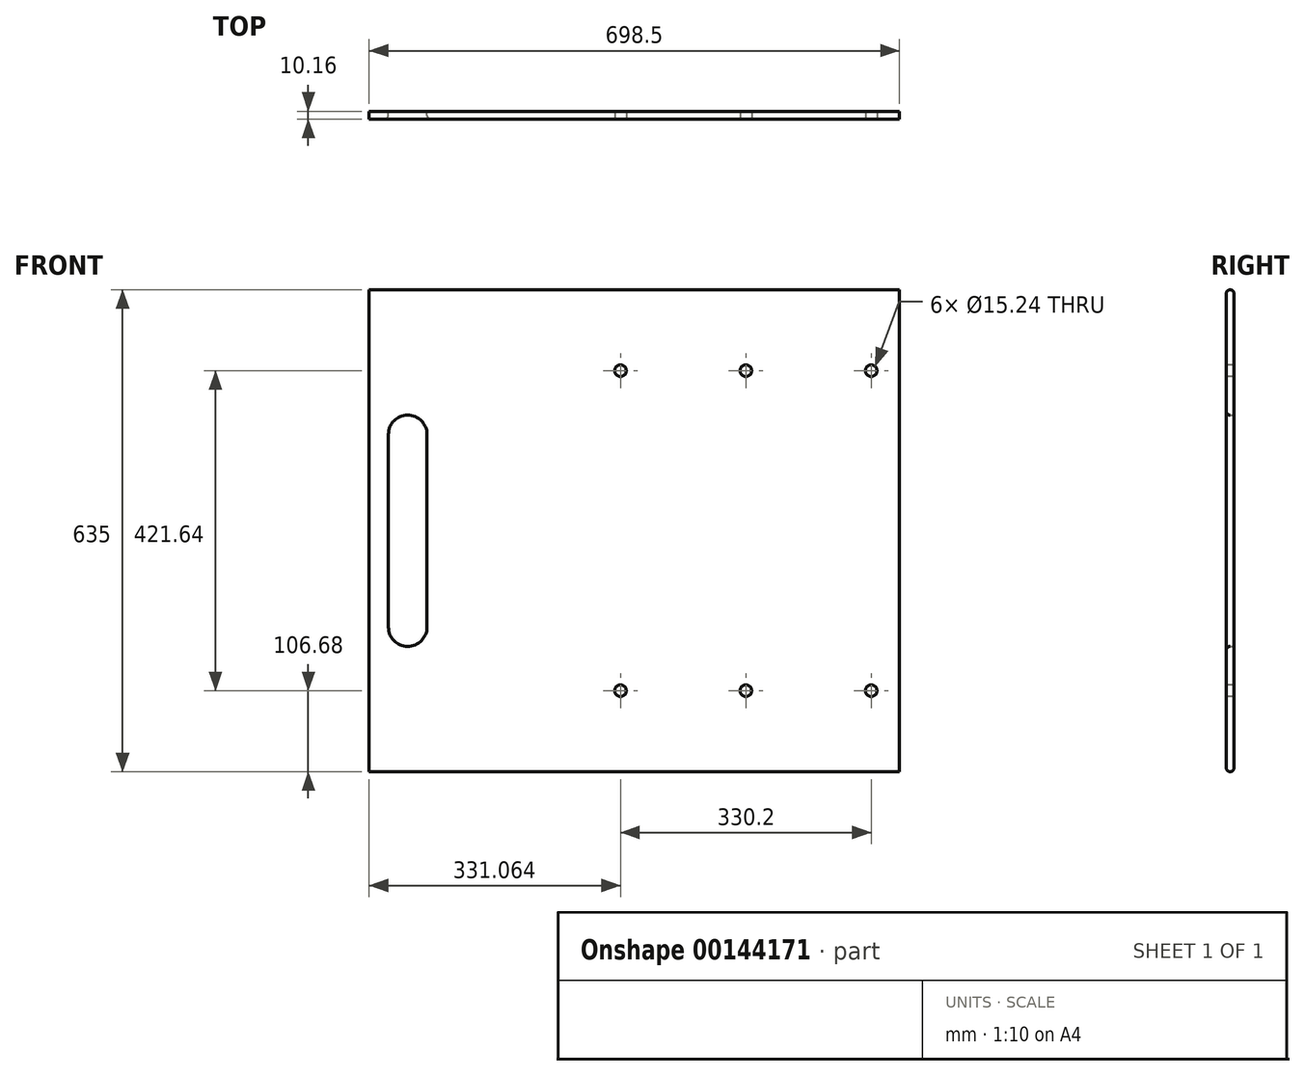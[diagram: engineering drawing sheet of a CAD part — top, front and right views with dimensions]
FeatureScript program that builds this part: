
annotation { "Feature Type Name" : "Feature", "Feature Type Description" : "" }
export const myFeature = defineFeature(function(context is Context, id is Id, definition is map)
    precondition{}
    {
        {
            var Q0;
            Q0=qCreatedBy(makeId("Front.planeOp"),FACE);
            var sketch = newSketch(context, id + "F0", { "sketchPlane" : qUnion([Q0])});
            skLineSegment(sketch, "E0.bottom", {"start": v(0, 0) * mm, "end": v(698.5, 0) * mm});
            skLineSegment(sketch, "E0.top", {"start": v(0, 635) * mm, "end": v(698.5, 635) * mm});
            skLineSegment(sketch, "E0.left", {"start": v(0, 0) * mm, "end": v(0, 635) * mm});
            skLineSegment(sketch, "E0.right", {"start": v(698.5, 0) * mm, "end": v(698.5, 635) * mm});
            skSolve(sketch);
        }
        {
            var Q0;
            Q0=makeQuery(id+"F0.imprint","IMPRINT",FACE,{"disambiguationData":[TD([[makeQuery(id+"F0.imprint","IMPRINT",EDGE,{"derivedFrom":sQuery(id+"F0.wireOp",EDGE,"E0.bottom")}),1.0]])]});
            extrude(context, id + "F1", {"entities" : qUnion([Q0]), "depth" : 10.16 * mm});
        }
        {
            var Q0;
            Q0=makeQuery(id+"F1.opExtrude","CAP_FACE",FACE,{"disambiguationData":[OSD([sQuery(id+"F0.wireOp",EDGE,"E0.bottom"),sQuery(id+"F0.wireOp",EDGE,"E0.top"),sQuery(id+"F0.wireOp",EDGE,"E0.left"),sQuery(id+"F0.wireOp",EDGE,"E0.right")])],"isStart":false});
            var sketch = newSketch(context, id + "F2", { "sketchPlane" : qUnion([Q0])});
            skLineSegment(sketch, "E1", {"start": v(0, 317.5) * mm, "end": v(50.8, 317.5) * mm, "construction": true});
            skLineSegment(sketch, "E2", {"start": v(50.8, 444.5) * mm, "end": v(50.8, 190.5) * mm, "construction": true});
            skArc(sketch, "E3.0.startCap", {"start": v(25.4, 444.5) * mm, "mid": v(50.8, 469.9) * mm, "end": v(76.2, 444.5) * mm});
            skArc(sketch, "E3.0.endCap", {"start": v(76.2, 190.5) * mm, "mid": v(50.8, 165.1) * mm, "end": v(25.4, 190.5) * mm});
            skLineSegment(sketch, "E3.0.left", {"start": v(76.2, 444.5) * mm, "end": v(76.2, 190.5) * mm});
            skLineSegment(sketch, "E3.0.right", {"start": v(25.4, 444.5) * mm, "end": v(25.4, 190.5) * mm});
            skSolve(sketch);
        }
        {
            var Q0;
            Q0=makeQuery(id+"F1.opExtrude","CAP_FACE",FACE,{"disambiguationData":[OSD([sQuery(id+"F0.wireOp",EDGE,"E0.bottom"),sQuery(id+"F0.wireOp",EDGE,"E0.top"),sQuery(id+"F0.wireOp",EDGE,"E0.left"),sQuery(id+"F0.wireOp",EDGE,"E0.right")])],"isStart":true});
            var sketch = newSketch(context, id + "F3", { "sketchPlane" : qUnion([Q0])});
            skLineSegment(sketch, "E4.0", {"start": v(-25.4, 444.5) * mm, "end": v(-25.4, 190.5) * mm});
            skArc(sketch, "E5.0", {"start": v(-25.4, 444.5) * mm, "mid": v(-50.8, 469.9) * mm, "end": v(-76.2, 444.5) * mm});
            skLineSegment(sketch, "E6.0", {"start": v(-76.2, 444.5) * mm, "end": v(-76.2, 190.5) * mm});
            skArc(sketch, "E7.0", {"start": v(-76.2, 190.5) * mm, "mid": v(-50.8, 165.1) * mm, "end": v(-25.4, 190.5) * mm});
            skSolve(sketch);
        }
        {
            var Q0;
            Q0=makeQuery(id+"F3.imprint","IMPRINT",FACE,{"disambiguationData":[TD([[makeQuery(id+"F3.imprint","IMPRINT",EDGE,{"derivedFrom":sQuery(id+"F3.wireOp",EDGE,"E4.0")}),-1.0]])]});
            extrude(context, id + "F4", {"entities" : qUnion([Q0]), "operationType" : NewBodyOperationType.REMOVE, "endBound" : BoundingType.THROUGH_ALL, "oppositeDirection" : true, "depth" : 25.4 * mm});
        }
        {
            var Q0;
            Q0=makeQuery(id+"F4.boolean.opBoolean","COPY",EDGE,{"derivedFrom":makeQuery(id+"F4.opExtrude","CAP_EDGE",EDGE,{"disambiguationData":[OSD([sQuery(id+"F3.wireOp",EDGE,"E7.0")])],"isStart":true})});
            var Q1;
            Q1=makeQuery(id+"F4.boolean.opBoolean","INTERSECT",EDGE,{"derivedFrom":[makeQuery(id+"F1.opExtrude","CAP_FACE",FACE,{"disambiguationData":[OSD([sQuery(id+"F0.wireOp",EDGE,"E0.bottom"),sQuery(id+"F0.wireOp",EDGE,"E0.top"),sQuery(id+"F0.wireOp",EDGE,"E0.left"),sQuery(id+"F0.wireOp",EDGE,"E0.right")])],"isStart":false}),makeQuery(id+"F4.opExtrude","SWEPT_FACE",FACE,{"disambiguationData":[OSD([sQuery(id+"F3.wireOp",EDGE,"E6.0")])]})]});
            fillet(context, id + "F5", {"entities" : qUnion([Q0, Q1]), "radius" : 5.08 * mm, "tangentPropagation" : true, "allowEdgeOverflow" : false});
        }
        {
            var Q0;
            Q0=makeQuery(id+"F1.opExtrude","CAP_EDGE",EDGE,{"disambiguationData":[OSD([sQuery(id+"F0.wireOp",EDGE,"E0.top")])],"isStart":false});
            var Q1;
            Q1=makeQuery(id+"F1.opExtrude","CAP_EDGE",EDGE,{"disambiguationData":[OSD([sQuery(id+"F0.wireOp",EDGE,"E0.top")])],"isStart":true});
            var Q2;
            Q2=makeQuery(id+"F1.opExtrude","CAP_EDGE",EDGE,{"disambiguationData":[OSD([sQuery(id+"F0.wireOp",EDGE,"E0.bottom")])],"isStart":false});
            var Q3;
            Q3=makeQuery(id+"F1.opExtrude","CAP_EDGE",EDGE,{"disambiguationData":[OSD([sQuery(id+"F0.wireOp",EDGE,"E0.bottom")])],"isStart":true});
            fillet(context, id + "F6", {"entities" : qUnion([Q0, Q1, Q2, Q3]), "radius" : 5.08 * mm, "tangentPropagation" : true, "allowEdgeOverflow" : false});
        }
        {
            var Q0;
            Q0=makeQuery(id+"F2.imprint","IMPRINT",FACE,{"disambiguationData":[TD([[makeQuery(id+"F2.imprint","IMPRINT",EDGE,{"derivedFrom":sQuery(id+"F2.wireOp",EDGE,"E3.0.startCap")}),1.0]])]});
            var sketch = newSketch(context, id + "F7", { "sketchPlane" : qUnion([Q0])});
            skLineSegment(sketch, "E8.0", {"start": v(698.5, 5.08) * mm, "end": v(698.5, 629.92) * mm});
            skPoint(sketch, "E9", {"position": v(661.26, 528.32) * mm});
            skPoint(sketch, "E10.1.0.0", {"position": v(496.16, 528.32) * mm});
            skPoint(sketch, "E10.2.0.0", {"position": v(331.06, 528.32) * mm});
            skLineSegment(sketch, "E10.direction1", {"start": v(661.26, 528.32) * mm, "end": v(496.16, 528.32) * mm, "construction": true});
            skPoint(sketch, "E11", {"position": v(661.26, 106.68) * mm});
            skPoint(sketch, "E12.1.0.0", {"position": v(496.16, 106.68) * mm});
            skPoint(sketch, "E12.2.0.0", {"position": v(331.06, 106.68) * mm});
            skLineSegment(sketch, "E12.direction1", {"start": v(661.26, 106.68) * mm, "end": v(496.16, 106.68) * mm, "construction": true});
            skSolve(sketch);
        }
        {
            var Q0;
            Q0=sQuery(id+"F7.wireOp",VERTEX,"E10.1.0.0");
            var Q1;
            Q1=sQuery(id+"F7.wireOp",VERTEX,"E10.2.0.0");
            var Q2;
            Q2=sQuery(id+"F7.wireOp",VERTEX,"E9");
            var Q3;
            Q3=sQuery(id+"F7.wireOp",VERTEX,"E11");
            var Q4;
            Q4=sQuery(id+"F7.wireOp",VERTEX,"E12.1.0.0");
            var Q5;
            Q5=sQuery(id+"F7.wireOp",VERTEX,"E12.2.0.0");
            var Q6;
            Q6=makeQuery(id+"F1.opExtrude","SWEPT_BODY",BODY,{"disambiguationData":[OSD([sQuery(id+"F0.wireOp",EDGE,"E0.bottom"),sQuery(id+"F0.wireOp",EDGE,"E0.top"),sQuery(id+"F0.wireOp",EDGE,"E0.left"),sQuery(id+"F0.wireOp",EDGE,"E0.right")])]});
            hole(context, id + "F8", {"style" : HoleStyle.SIMPLE, "endStyle" : HoleEndStyle.THROUGH, "holeDiameter" : 15.24 * mm, "locations" : qUnion([Q0, Q1, Q2, Q3, Q4, Q5]), "scope" : qUnion([Q6]), "isTappedThrough" : true});
        }
    });
